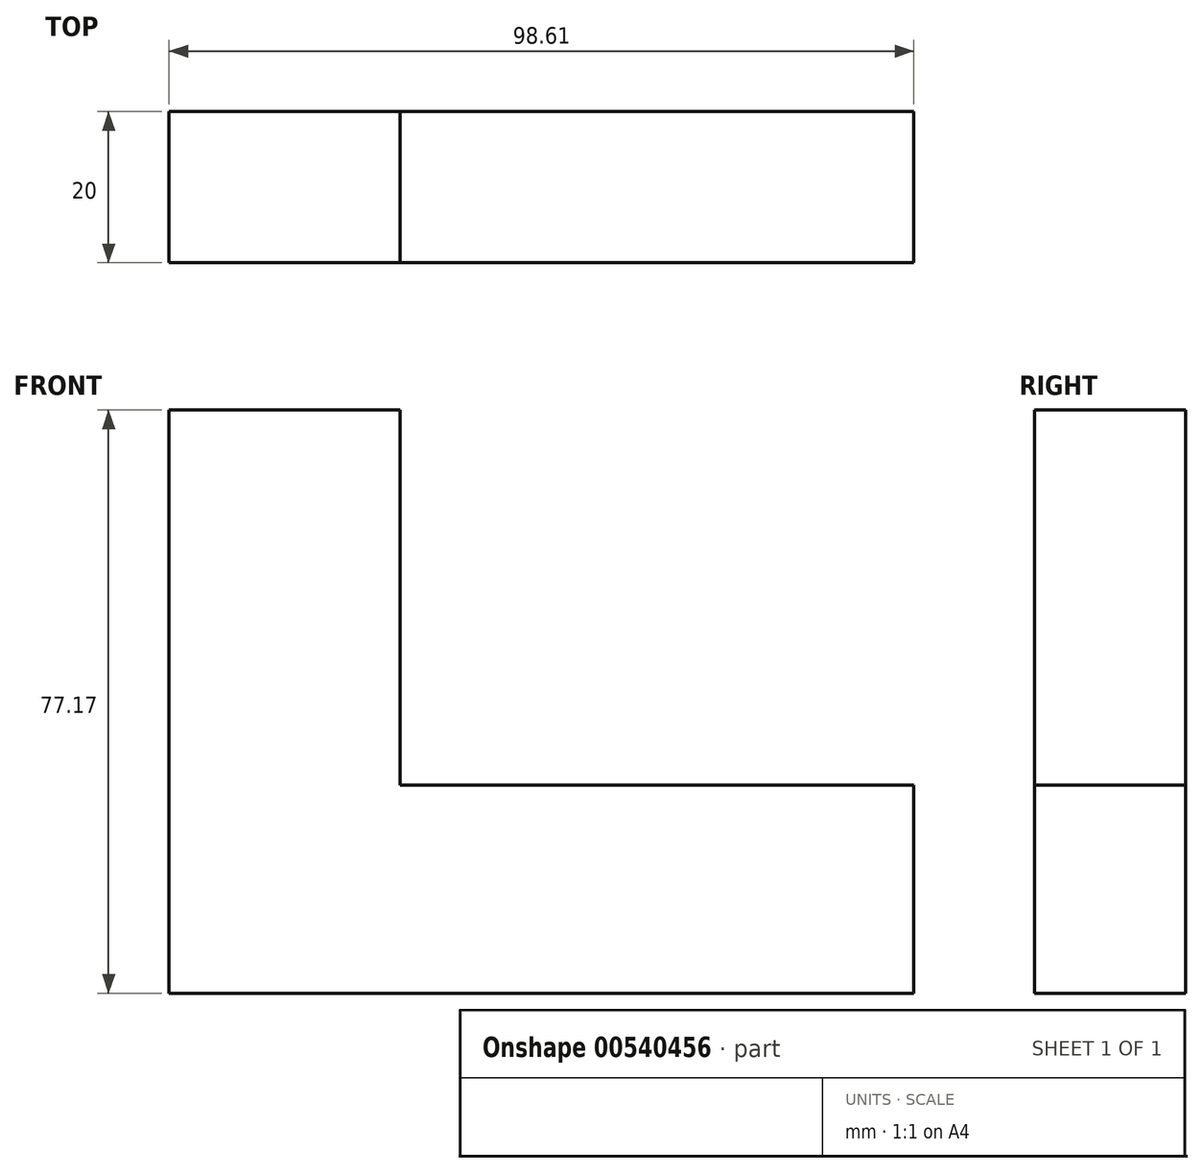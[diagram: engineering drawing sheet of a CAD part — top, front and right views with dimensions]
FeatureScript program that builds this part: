
annotation { "Feature Type Name" : "Feature", "Feature Type Description" : "" }
export const myFeature = defineFeature(function(context is Context, id is Id, definition is map)
    precondition{}
    {
        {
            var Q0;
            Q0=qCreatedBy(makeId("Front.planeOp"),FACE);
            var sketch = newSketch(context, id + "F0", { "sketchPlane" : qUnion([Q0])});
            skLineSegment(sketch, "E0.bottom", {"start": v(0, 0) * mm, "end": v(-30.57, 0) * mm});
            skLineSegment(sketch, "E0.top", {"start": v(0, 77.17) * mm, "end": v(-30.57, 77.17) * mm});
            skLineSegment(sketch, "E0.left", {"start": v(0, 0) * mm, "end": v(0, 77.17) * mm});
            skLineSegment(sketch, "E0.right", {"start": v(-30.57, 0) * mm, "end": v(-30.57, 77.17) * mm});
            skLineSegment(sketch, "E1.bottom", {"start": v(68.04, 27.54) * mm, "end": v(0, 27.54) * mm});
            skLineSegment(sketch, "E1.top", {"start": v(68.04, 0) * mm, "end": v(0, 0) * mm});
            skLineSegment(sketch, "E1.left", {"start": v(68.04, 27.54) * mm, "end": v(68.04, 0) * mm});
            skLineSegment(sketch, "E1.right", {"start": v(0, 27.54) * mm, "end": v(0, 0) * mm});
            skSolve(sketch);
        }
        {
            var Q0;
            Q0=makeQuery(id+"F0.imprint","IMPRINT",FACE,{"disambiguationData":[TD([[makeQuery(id+"F0.imprint","IMPRINT",EDGE,{"derivedFrom":sQuery(id+"F0.wireOp",EDGE,"E0.bottom")}),-1.0]])]});
            var Q1;
            Q1=makeQuery(id+"F0.imprint","IMPRINT",FACE,{"disambiguationData":[TD([[makeQuery(id+"F0.imprint","IMPRINT",EDGE,{"derivedFrom":sQuery(id+"F0.wireOp",EDGE,"E1.bottom")}),1.0]])]});
            extrude(context, id + "F1", {"entities" : qUnion([Q0, Q1]), "depth" : 20 * mm, "offsetDistance" : 25 * mm});
        }
    });
